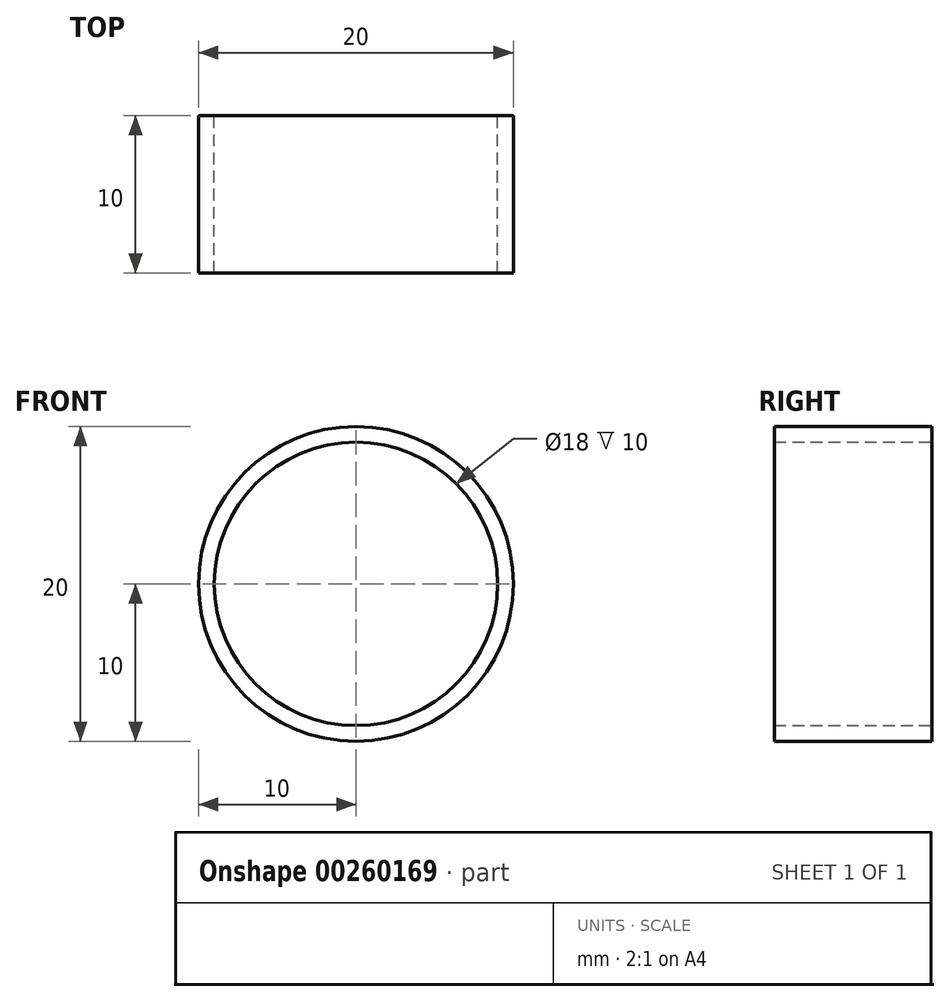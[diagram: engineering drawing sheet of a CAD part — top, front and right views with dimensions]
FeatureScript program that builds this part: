
annotation { "Feature Type Name" : "Feature", "Feature Type Description" : "" }
export const myFeature = defineFeature(function(context is Context, id is Id, definition is map)
    precondition{}
    {
        {
            var Q0;
            Q0=qCreatedBy(makeId("Front.planeOp"),FACE);
            var sketch = newSketch(context, id + "F0", { "sketchPlane" : qUnion([Q0])});
            skCircle(sketch, "E0", {"center": v(0, 0) * mm, "radius": 10 * mm});
            skCircle(sketch, "E1", {"center": v(0, 0) * mm, "radius": 9 * mm});
            skSolve(sketch);
        }
        {
            var Q0;
            Q0=makeQuery(id+"F0.imprint","IMPRINT",FACE,{"disambiguationData":[TD([[makeQuery(id+"F0.imprint","IMPRINT",EDGE,{"derivedFrom":sQuery(id+"F0.wireOp",EDGE,"E0")}),1.0]])]});
            extrude(context, id + "F1", {"entities" : qUnion([Q0]), "endBound" : BoundingType.SYMMETRIC, "depth" : 10 * mm});
        }
    });
